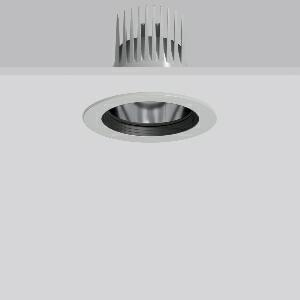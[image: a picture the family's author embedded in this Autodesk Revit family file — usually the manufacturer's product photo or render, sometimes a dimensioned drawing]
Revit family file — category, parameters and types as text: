
# Revit family: heledon_maxi_e_901766_004_3_76_14cb
name_source: partatom
category: Lighting Fixtures
units: mm (PartAtom-declared; Revit-internal decimal feet)

## family parameters
Cut with Voids When Loaded = No
Host = Face
Light Source = No
Part Type = Normal
Room Calculation Point = No
Round Connector Dimension = Use Diameter
Shared = No

## types (1)
- HELEDON maxi E (1 x LED Modul 935, 4200 lm, 3500)
    Apparent Load = 35 VA
    Approval mark = CE
    CIE Flux Codes = 97 100 100 100 100
    Color Rendering = 92
    Color Temperature = 3500
    Default Elevation = 1800 mm
    Description = Series: HELEDON maxi
Round recessed downlight. Housing: die-cast aluminium, powder-coated. Black plastic ring and recessed LED to prevent glare from the side. Optical assembly with reflector made of MIRO-Silver with 98% total light reflection for outstanding efficiency - can be changed without tools. Best colour rendering index Ra>90. Suitable for Recessed ceiling mounting. Installation without tools thanks to spring fastening system. Including separate LED converter with connecting cable 600 mm.High quality converter without flickering and stroboscopic effect. Through-wiring box (5 pole) available as accessory. The following accessories can be mounted without use of tools: interchangeable lenses, decorative glasses, honeycomb louvre, clear and frosted diffusers, white interchangeable plastic ring. 
Colour: silver
Diameter: 162 mm
Height: 3 mm
Cut-out diameter: 152 mm
Recess height: 200 mm
Luminaire: recess height: 135 mm
Lamp: LED
Socket: without socket
Colour temperature: 3500K
Colour rendering index (CRI): 92
System power: 35 W
Rated luminous flux: 4200 lm
Luminous efficiency: 120 lm/W
Control gear: Converter, dimmable, DALI
Protection class: II
Type of protection: IP 20
    Height = 0 mm  [stored 0 ft]
    Lamp = 1 x LED Modul 935
    Lamp Light Flux = 4200 lm
    Lamp count = 1
    Length = 162 mm
    Lifetime = 50000 h
    Luminous efficacy = 120 lm/W
    Manufacturer = RZB
    ModVariant = No
    Model = 901766.004.3.76
    Mounting Place = Ceiling
    Mounting Type = Recessed
    Number of Poles = 1
    OnlyDefault = Yes
    Power Factor = 1
    Product Name = HELEDON maxi E
    Product group = Recessed downlights
    ProductGroupID = 402
    Protection Class = Protection class II
    Protection Degree = IP 20
    RLX_Detail_Level = 1
    RLX_Emergency_Light_Flux = 0 lm
    RLX_Emergency_Type = 0
    RLX_Emergency_Type_DB = No
    RlxData = <blob elided: 119513 chars, md5=4f3c678c>
    Socket = socket
    Standby Power = 0 W
    System Light Flux = 4200 lm
    System Power = 35 W
    Type Comments = Product without accessories
    Type Image = 901662.004.jpg
    URL = http://relux.com
    VarID = ---
    Voltage = 230 V
    Voltage Range = 220-240 V
    Weight = 0.00 kg
    Width = 0 mm  [stored 0 ft]

note: [stored X ft] marks values corroborated as IEEE doubles in the binary element streams (Revit-internal decimal feet)

## geometry (parser evidence)
native form markers: Blend x4, Sweep x11
no freeform markers — native parametric forms only
